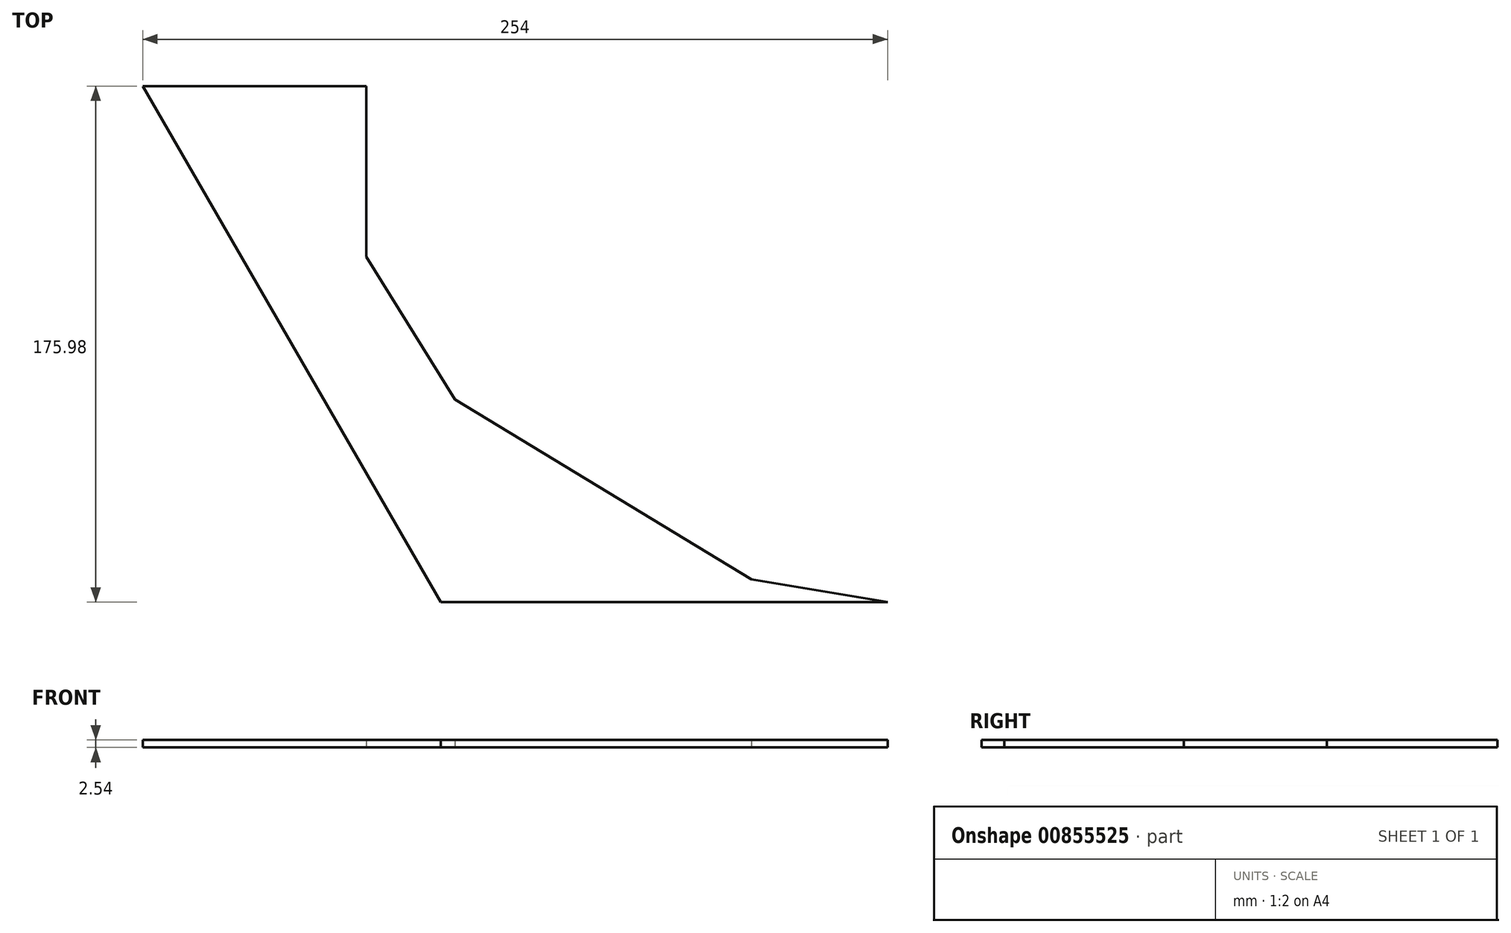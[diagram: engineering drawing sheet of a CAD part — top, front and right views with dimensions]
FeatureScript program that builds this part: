
annotation { "Feature Type Name" : "Feature", "Feature Type Description" : "" }
export const myFeature = defineFeature(function(context is Context, id is Id, definition is map)
    precondition{}
    {
        {
            var Q0;
            Q0=qCreatedBy(makeId("Top.planeOp"),FACE);
            var sketch = newSketch(context, id + "F0", { "sketchPlane" : qUnion([Q0])});
            skLineSegment(sketch, "E0", {"start": v(0, 0) * mm, "end": v(-101.6, 175.98) * mm});
            skLineSegment(sketch, "E1", {"start": v(0, 0) * mm, "end": v(152.4, 0) * mm});
            skLineSegment(sketch, "E2", {"start": v(-101.6, 175.98) * mm, "end": v(-25.4, 175.98) * mm});
            skLineSegment(sketch, "E3", {"start": v(-25.4, 175.98) * mm, "end": v(-25.4, 117.71) * mm});
            skLineSegment(sketch, "E4", {"start": v(-25.4, 117.71) * mm, "end": v(4.92, 69.07) * mm});
            skLineSegment(sketch, "E5", {"start": v(4.92, 69.07) * mm, "end": v(106, 7.8) * mm});
            skLineSegment(sketch, "E6", {"start": v(106, 7.8) * mm, "end": v(152.4, 0) * mm});
            skSolve(sketch);
        }
        {
            var Q0;
            Q0=makeQuery(id+"F0.imprint","IMPRINT",FACE,{"disambiguationData":[TD([[makeQuery(id+"F0.imprint","IMPRINT",EDGE,{"derivedFrom":sQuery(id+"F0.wireOp",EDGE,"E0")}),-1.0]])]});
            extrude(context, id + "F1", {"entities" : qUnion([Q0]), "depth" : 2.54 * mm, "offsetDistance" : 25.4 * mm});
        }
    });
